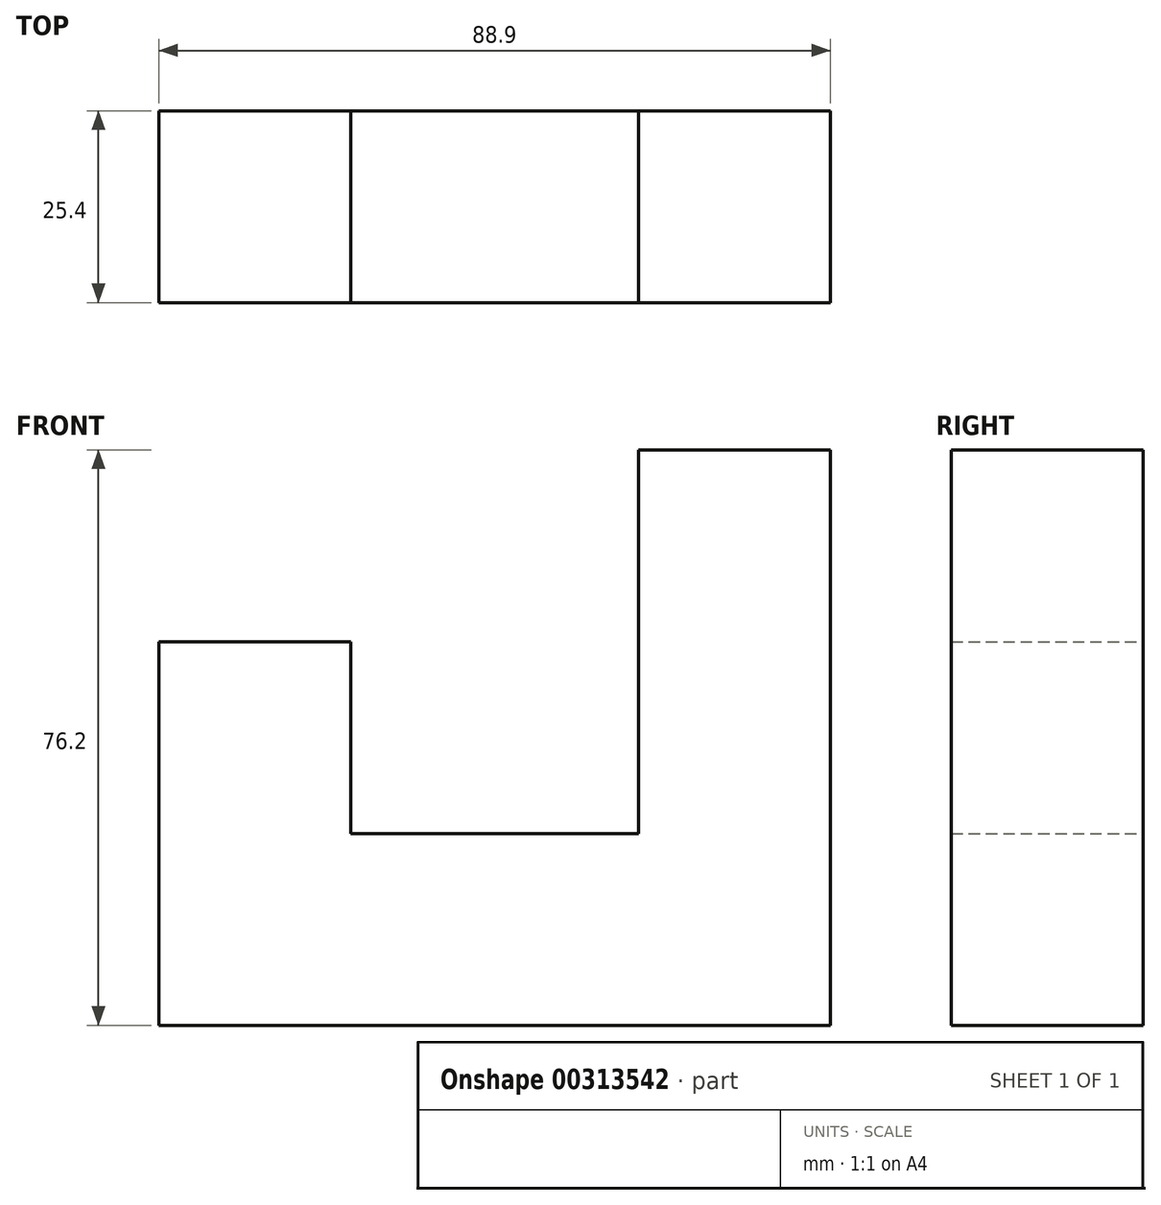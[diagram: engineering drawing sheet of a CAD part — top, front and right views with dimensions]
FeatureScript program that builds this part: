
annotation { "Feature Type Name" : "Feature", "Feature Type Description" : "" }
export const myFeature = defineFeature(function(context is Context, id is Id, definition is map)
    precondition{}
    {
        {
            var Q0;
            Q0=qCreatedBy(makeId("Front.planeOp"),FACE);
            var sketch = newSketch(context, id + "F0", { "sketchPlane" : qUnion([Q0])});
            skLineSegment(sketch, "E0", {"start": v(-46.93, -45.55) * mm, "end": v(41.97, -45.55) * mm});
            skLineSegment(sketch, "E1", {"start": v(41.97, -45.55) * mm, "end": v(41.97, 30.65) * mm});
            skLineSegment(sketch, "E2", {"start": v(41.97, 30.65) * mm, "end": v(16.57, 30.65) * mm});
            skLineSegment(sketch, "E3", {"start": v(16.57, 30.65) * mm, "end": v(16.57, -20.15) * mm});
            skLineSegment(sketch, "E4", {"start": v(16.57, -20.15) * mm, "end": v(-21.53, -20.15) * mm});
            skLineSegment(sketch, "E5", {"start": v(-21.53, -20.15) * mm, "end": v(-21.53, 5.25) * mm});
            skLineSegment(sketch, "E6", {"start": v(-21.53, 5.25) * mm, "end": v(-46.93, 5.25) * mm});
            skLineSegment(sketch, "E7", {"start": v(-46.93, 5.25) * mm, "end": v(-46.93, -45.55) * mm});
            skSolve(sketch);
        }
        {
            var Q0;
            Q0 = qSketchRegion(id + "F0", true);
            extrude(context, id + "F1", {"entities" : qUnion([Q0]), "depth" : 25.4 * mm});
        }
    });
